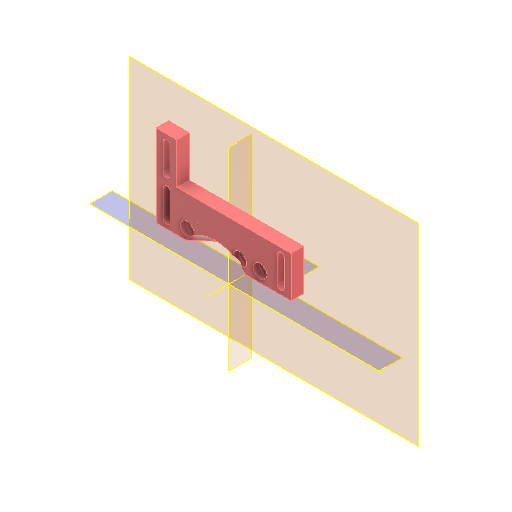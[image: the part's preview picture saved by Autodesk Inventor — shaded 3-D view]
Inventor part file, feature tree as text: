
AUTODESK INVENTOR PART (.ipt)
format: ipt  version: 2022 (Build 260153000, 153)  size: 261,632 bytes
history: native  units: mm
features: other x12, reference x10, plane x8, sketch x5, extrude x4, projected_geometry x2, hole x1, revolve x1
ambient origin geometry x8: Origin, YZ Plane, XZ Plane, XY Plane, X Axis, Y Axis, Z Axis, Center Point
bodies: Volumenkörper1 (feature_tree)
feature tree (43):
  plane  "Arbeitsebene1"
  plane  "Arbeitsebene2"
  extrude  "Extrusion1"  Depth=38.0mm
  hole  "Bohrung1"  [1 undecoded]
  sketch  "Skizze3"  dims[d2=2.9mm d3=6.0mm d4=6.5mm d5=3.0mm d6=90.0deg d7=8.0mm d8=20.594885mm d9=38.0mm]
  other  "Arbeitspunkt1"
  plane  "Arbeitsebene4"
  plane  "Arbeitsebene5"
  extrude  "Extrusion2"  Depth=10.0mm
  plane  "Arbeitsebene3"
  other  "Arbeitsachse1"
  revolve  "Umdrehung1"
  plane  "Arbeitsebene8"
  extrude  "Extrusion5"  Depth=10.0mm
  extrude  "Extrusion6"  Depth=10.0mm
  reference  "Referenz1"
  reference  "Referenz3"
  reference  "Referenz4"
  sketch  "Skizze2"  dims[d0=10.0mm d1=0.0mm]
  reference  "Referenz5"
  reference  "Referenz6"
  reference  "Referenz7"
  projected_geometry  "Projizierte Kontur1"
  reference  "Referenz8"
  reference  "Referenz9"
  plane  "Arbeitsebene6"
  plane  "Arbeitsebene7"
  sketch  "Skizze7"  dims[d10=10.0mm d11=10.0mm]
  reference  "Referenz17"
  sketch  "Skizze8"  dims[d12=10.0mm d13=10.0mm]
  reference  "Referenz18"
  sketch  "Skizze9"  dims[d14=6.0mm d15=0.0mm d30=10.0mm d31=10.0mm d32=10.0mm d33=10.0mm d34=6.5mm d35=3.2mm d36=6.5mm d37=3.2mm d47=11.8mm d49=20.0mm d50=6.5mm d51=3.2mm d52=25.0mm d53=90.0deg d54=0.1mm d55=12.5mm d56=0.0mm d57=5.0mm d58=0.0mm d59=0.0mm]
  projected_geometry  "Projizierte Kontur3"
  other  "Assemlby_Scanner_v1.iam"
  other  "00_CCTV_lens_M12_25mm_5mp:1"
  other  "Assemlby_lightsheet_generator_passive_v2.iam"
  other  "30_Lightsheet_generator_passive_lid_v0:1"
  other  "Assembly_Guinardia_V4.iam"
  other  "10_Wellplate_base_v3:1"
  other  "00_Thorlabs_LJ1878L1-A-Step:1"
  other  "30_Scanlens_Laseradaper_v1:1"
  other  "Assembly_Guinardia_V2.iam"
  other  "10_Wellplate_base_v2:1"
note: 1 required parameter value undecoded (feature->parameter linkage not recoverable at this tier; creation-order binding heuristic only, values carry confidence <= 0.55)
